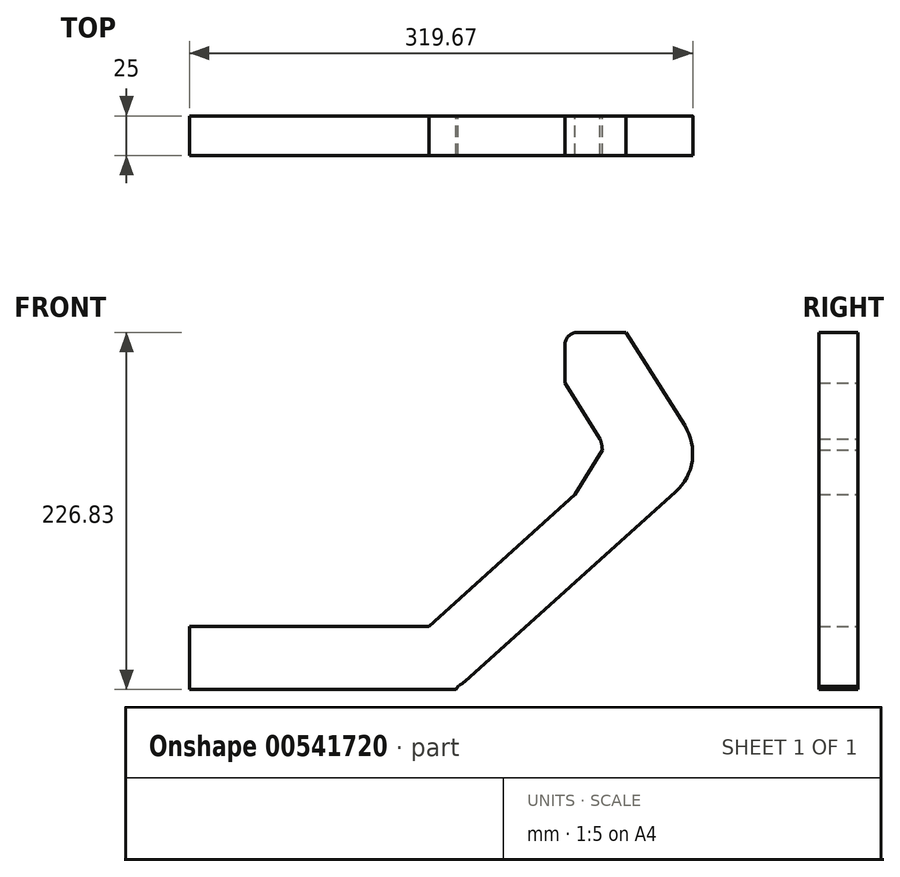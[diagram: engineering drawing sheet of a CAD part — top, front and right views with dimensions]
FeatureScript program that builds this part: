
annotation { "Feature Type Name" : "Feature", "Feature Type Description" : "" }
export const myFeature = defineFeature(function(context is Context, id is Id, definition is map)
    precondition{}
    {
        {
            var Q0;
            Q0=qCreatedBy(makeId("Front.planeOp"),FACE);
            var sketch = newSketch(context, id + "F0", { "sketchPlane" : qUnion([Q0])});
            skLineSegment(sketch, "E0.bottom", {"start": v(-269.45, -33.9) * mm, "end": v(-421.5, -33.9) * mm});
            skLineSegment(sketch, "E0.top", {"start": v(-252.3, -73.9) * mm, "end": v(-421.5, -73.9) * mm});
            skPoint(sketch, "E0.middle", {"position": v(-382.53, -53.9) * mm});
            skLineSegment(sketch, "E1.top", {"start": v(-269.45, -73.9) * mm, "end": v(-259.97, -73.9) * mm});
            skPoint(sketch, "E2.visualSharp", {"position": v(-232.3, -73.9) * mm});
            skLineSegment(sketch, "E3", {"start": v(-246.6, -68.77) * mm, "end": v(-112.76, 51.57) * mm});
            skLineSegment(sketch, "E4", {"start": v(-167.44, 58.34) * mm, "end": v(-269.45, -33.9) * mm});
            skPoint(sketch, "E5.visualSharp", {"position": v(-252.3, -73.9) * mm});
            skArc(sketch, "E5.filletArc", {"start": v(-259.97, -73.9) * mm, "mid": v(-252.8, -72.57) * mm, "end": v(-246.6, -68.77) * mm});
            skPoint(sketch, "E6.visualSharp", {"position": v(-155.11, 69.48) * mm});
            skArc(sketch, "E6.filletArc", {"start": v(-167.44, 58.34) * mm, "mid": v(-159.97, 70.72) * mm, "end": v(-160.6, 85.16) * mm});
            skPoint(sketch, "E7.visualSharp", {"position": v(-92.84, 69.48) * mm});
            skArc(sketch, "E7.filletArc", {"start": v(-112.76, 51.57) * mm, "mid": v(-102.14, 71.56) * mm, "end": v(-106.9, 93.7) * mm});
            skLineSegment(sketch, "E8", {"start": v(-106.9, 93.7) * mm, "end": v(-144.2, 152.93) * mm});
            skLineSegment(sketch, "E9", {"start": v(-160.6, 85.16) * mm, "end": v(-183.07, 120.83) * mm});
            skLineSegment(sketch, "E10.bottom", {"start": v(-144.2, 152.93) * mm, "end": v(-175.07, 152.93) * mm});
            skLineSegment(sketch, "E10.top", {"start": v(-144.2, 120.83) * mm, "end": v(-183.07, 120.83) * mm});
            skLineSegment(sketch, "E10.left", {"start": v(-144.2, 152.93) * mm, "end": v(-144.2, 120.83) * mm});
            skLineSegment(sketch, "E10.right", {"start": v(-183.07, 144.93) * mm, "end": v(-183.07, 120.83) * mm});
            skPoint(sketch, "E11.visualSharp", {"position": v(-183.07, 152.93) * mm});
            skArc(sketch, "E11.filletArc", {"start": v(-175.07, 152.93) * mm, "mid": v(-180.73, 150.6) * mm, "end": v(-183.07, 144.93) * mm});
            skPoint(sketch, "E12.end.orphan", {"position": v(-628.61, -73.9) * mm});
            skLineSegment(sketch, "E13", {"start": v(-421.5, -33.9) * mm, "end": v(-421.5, -73.9) * mm});
            skPoint(sketch, "E14.orphan", {"position": v(-532.76, -33.9) * mm});
            skPoint(sketch, "E15.orphan", {"position": v(-532.76, -73.9) * mm});
            skLineSegment(sketch, "E16", {"start": v(-269.45, -33.9) * mm, "end": v(-205.35, 94.26) * mm});
            skLineSegment(sketch, "E17", {"start": v(-252.3, -73.9) * mm, "end": v(-155.11, 85.16) * mm});
            skSolve(sketch);
        }
        {
            var Q0;
            Q0 = qSketchRegion(id + "F0", true);
            extrude(context, id + "F1", {"entities" : qUnion([Q0]), "endBound" : BoundingType.SYMMETRIC, "depth" : 25 * mm, "offsetDistance" : 25 * mm});
        }
    });
